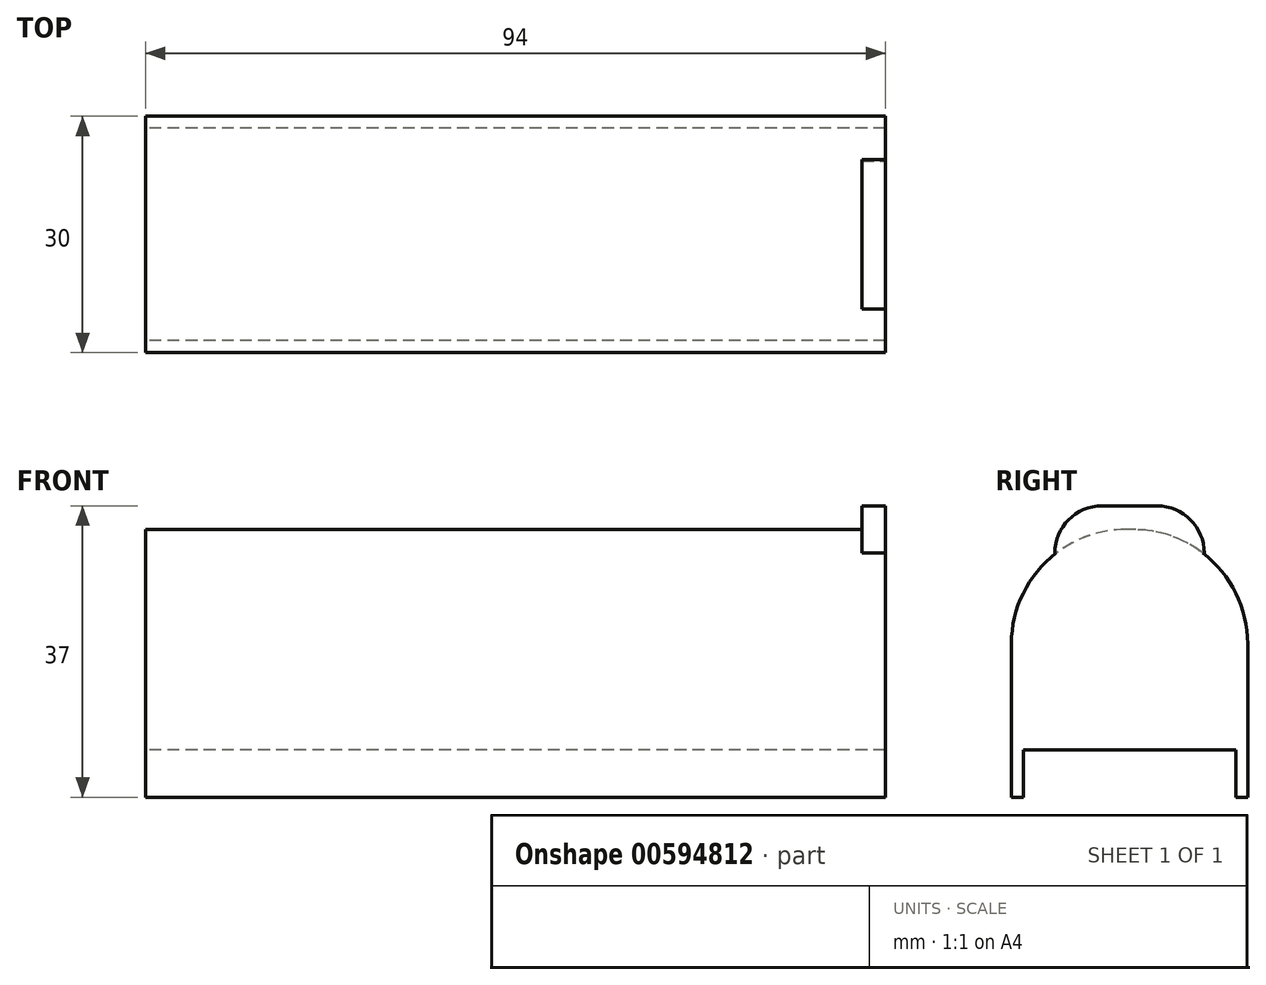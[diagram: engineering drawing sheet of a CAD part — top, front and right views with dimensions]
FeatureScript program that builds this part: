
annotation { "Feature Type Name" : "Feature", "Feature Type Description" : "" }
export const myFeature = defineFeature(function(context is Context, id is Id, definition is map)
    precondition{}
    {
        {
            var Q0;
            Q0=qCreatedBy(makeId("Top.planeOp"),FACE);
            var sketch = newSketch(context, id + "F0", { "sketchPlane" : qUnion([Q0])});
            skLineSegment(sketch, "E0.bottom", {"start": v(0, 0) * mm, "end": v(94, 0) * mm});
            skLineSegment(sketch, "E0.top", {"start": v(0, -30) * mm, "end": v(94, -30) * mm});
            skLineSegment(sketch, "E0.left", {"start": v(0, 0) * mm, "end": v(0, -30) * mm});
            skLineSegment(sketch, "E0.right", {"start": v(94, 0) * mm, "end": v(94, -30) * mm});
            skSolve(sketch);
        }
        {
            var Q0;
            Q0=makeQuery(id+"F0.imprint","IMPRINT",FACE,{"disambiguationData":[TD([[makeQuery(id+"F0.imprint","IMPRINT",EDGE,{"derivedFrom":sQuery(id+"F0.wireOp",EDGE,"E0.bottom")}),-1.0]])]});
            extrude(context, id + "F1", {"entities" : qUnion([Q0]), "depth" : 28 * mm, "offsetDistance" : 25 * mm});
        }
        {
            var Q0;
            Q0=makeQuery(id+"F1.opExtrude","CAP_FACE",FACE,{"disambiguationData":[OSD([sQuery(id+"F0.wireOp",EDGE,"E0.bottom"),sQuery(id+"F0.wireOp",EDGE,"E0.top"),sQuery(id+"F0.wireOp",EDGE,"E0.left"),sQuery(id+"F0.wireOp",EDGE,"E0.right")])],"isStart":true});
            var sketch = newSketch(context, id + "F2", { "sketchPlane" : qUnion([Q0])});
            skLineSegment(sketch, "E1.bottom", {"start": v(94, 0) * mm, "end": v(0, 0) * mm});
            skLineSegment(sketch, "E1.top", {"start": v(94, 1.5) * mm, "end": v(0, 1.5) * mm});
            skLineSegment(sketch, "E1.left", {"start": v(94, 0) * mm, "end": v(94, 1.5) * mm});
            skLineSegment(sketch, "E1.right", {"start": v(0, 0) * mm, "end": v(0, 1.5) * mm});
            skLineSegment(sketch, "E2.bottom", {"start": v(94, 30) * mm, "end": v(0, 30) * mm});
            skLineSegment(sketch, "E2.top", {"start": v(94, 28.5) * mm, "end": v(0, 28.5) * mm});
            skLineSegment(sketch, "E2.left", {"start": v(94, 30) * mm, "end": v(94, 28.5) * mm});
            skLineSegment(sketch, "E2.right", {"start": v(0, 30) * mm, "end": v(0, 28.5) * mm});
            skSolve(sketch);
        }
        {
            var Q0;
            Q0=makeQuery(id+"F2.imprint","IMPRINT",FACE,{"disambiguationData":[TD([[makeQuery(id+"F2.imprint","IMPRINT",EDGE,{"derivedFrom":sQuery(id+"F2.wireOp",EDGE,"E1.bottom")}),1.0]])]});
            var Q1;
            Q1=makeQuery(id+"F2.imprint","IMPRINT",FACE,{"disambiguationData":[TD([[makeQuery(id+"F2.imprint","IMPRINT",EDGE,{"derivedFrom":sQuery(id+"F2.wireOp",EDGE,"E2.bottom")}),-1.0]])]});
            extrude(context, id + "F3", {"entities" : qUnion([Q0, Q1]), "operationType" : NewBodyOperationType.ADD, "depth" : 6 * mm, "offsetDistance" : 25 * mm});
        }
        {
            var Q0;
            Q0=makeQuery(id+"F1.opExtrude","CAP_EDGE",EDGE,{"disambiguationData":[OSD([sQuery(id+"F0.wireOp",EDGE,"E0.bottom")])],"isStart":false});
            var Q1;
            Q1=makeQuery(id+"F1.opExtrude","CAP_EDGE",EDGE,{"disambiguationData":[OSD([sQuery(id+"F0.wireOp",EDGE,"E0.top")])],"isStart":false});
            fillet(context, id + "F4", {"entities" : qUnion([Q0, Q1]), "radius" : 14.5 * mm, "tangentPropagation" : true, "allowEdgeOverflow" : false});
        }
        {
            var Q0;
            Q0=makeQuery(id+"F3.boolean.opBoolean","MERGE",FACE,{"derivedFrom":[makeQuery(id+"F1.opExtrude","SWEPT_FACE",FACE,{"disambiguationData":[OSD([sQuery(id+"F0.wireOp",EDGE,"E0.right")])]}),makeQuery(id+"F3.opExtrude","SWEPT_FACE",FACE,{"disambiguationData":[OSD([sQuery(id+"F2.wireOp",EDGE,"E1.left")])]}),makeQuery(id+"F3.opExtrude","SWEPT_FACE",FACE,{"disambiguationData":[OSD([sQuery(id+"F2.wireOp",EDGE,"E2.left")])]})]});
            var sketch = newSketch(context, id + "F5", { "sketchPlane" : qUnion([Q0])});
            skPoint(sketch, "E3.middle", {"position": v(-15.5, 28) * mm});
            skLineSegment(sketch, "E4", {"start": v(-15, 28) * mm, "end": v(-14.5, 0) * mm, "construction": true});
            skLineSegment(sketch, "E5.bottom", {"start": v(-24.5, 31) * mm, "end": v(-5.5, 31) * mm});
            skLineSegment(sketch, "E5.top", {"start": v(-24.5, 25) * mm, "end": v(-5.5, 25) * mm});
            skLineSegment(sketch, "E5.left", {"start": v(-24.5, 31) * mm, "end": v(-24.5, 25) * mm});
            skLineSegment(sketch, "E5.right", {"start": v(-5.5, 31) * mm, "end": v(-5.5, 25) * mm});
            skPoint(sketch, "E5.middle", {"position": v(-15, 28) * mm});
            skSolve(sketch);
        }
        {
            var Q0;
            Q0=makeQuery(id+"F5.imprint","IMPRINT",FACE,{"disambiguationData":[TD([[makeQuery(id+"F5.imprint","IMPRINT",EDGE,{"derivedFrom":sQuery(id+"F5.wireOp",EDGE,"E5.bottom")}),-1.0]])]});
            extrude(context, id + "F6", {"entities" : qUnion([Q0]), "operationType" : NewBodyOperationType.ADD, "oppositeDirection" : true, "depth" : 3 * mm, "offsetDistance" : 25 * mm});
        }
        {
            var Q0;
            Q0=makeQuery(id+"F6.opExtrude","SWEPT_EDGE",EDGE,{"disambiguationData":[OSD([sQuery(id+"F5.wireOp",EDGE,"E5.bottom"),sQuery(id+"F5.wireOp",EDGE,"E5.left")])]});
            var Q1;
            Q1=makeQuery(id+"F6.opExtrude","SWEPT_EDGE",EDGE,{"disambiguationData":[OSD([sQuery(id+"F5.wireOp",EDGE,"E5.bottom"),sQuery(id+"F5.wireOp",EDGE,"E5.right")])]});
            fillet(context, id + "F7", {"entities" : qUnion([Q0, Q1]), "radius" : 6 * mm, "tangentPropagation" : true, "allowEdgeOverflow" : false});
        }
    });
